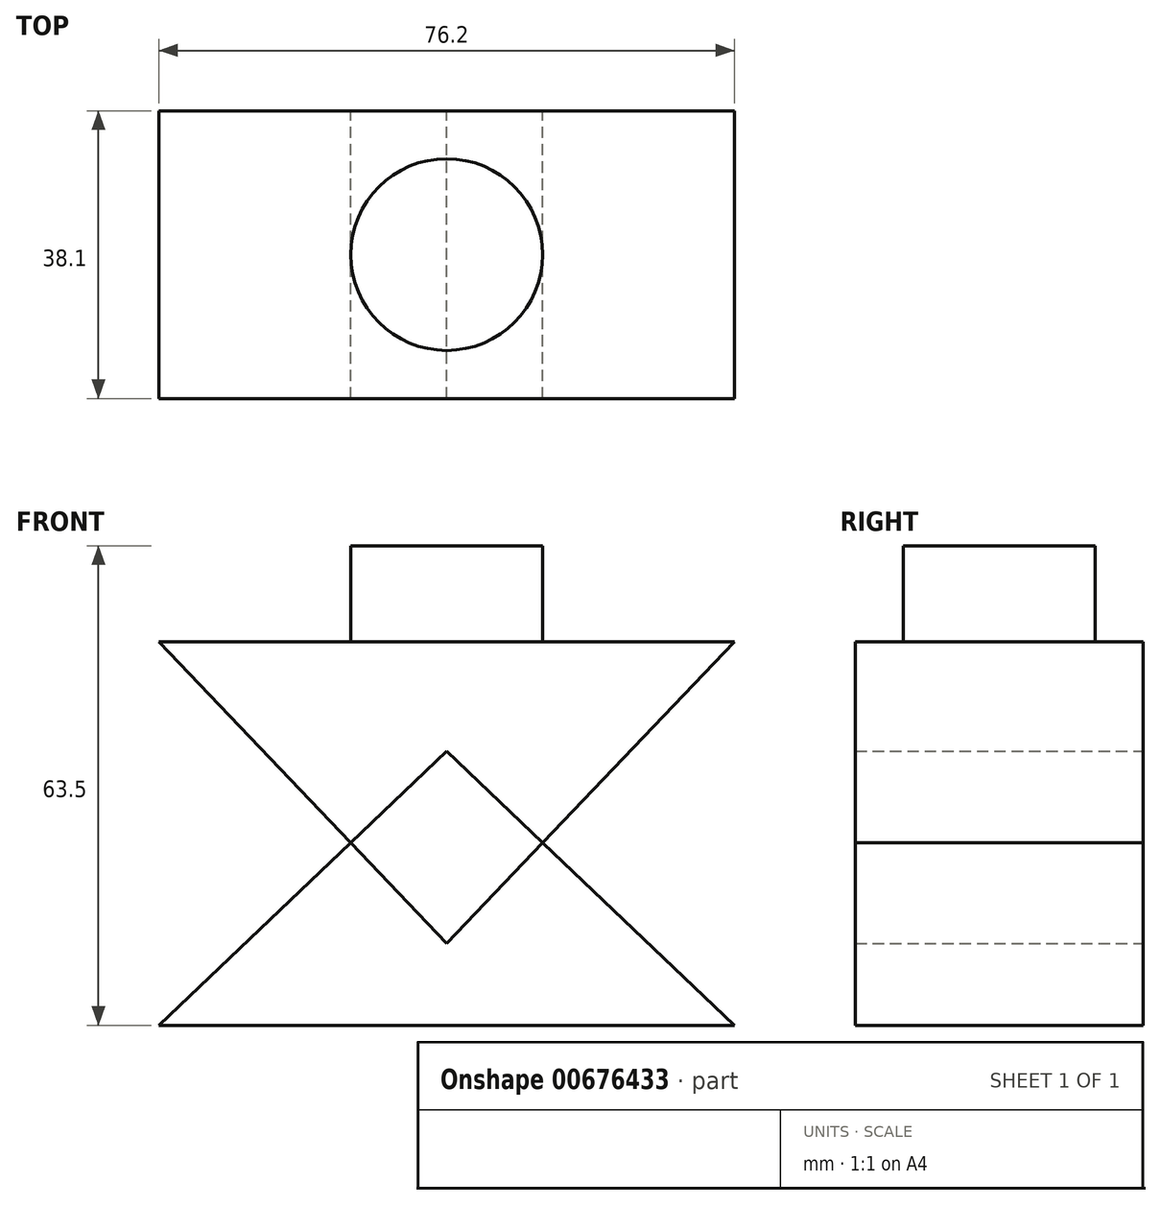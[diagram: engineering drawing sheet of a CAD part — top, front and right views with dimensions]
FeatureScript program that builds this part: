
annotation { "Feature Type Name" : "Feature", "Feature Type Description" : "" }
export const myFeature = defineFeature(function(context is Context, id is Id, definition is map)
    precondition{}
    {
        {
            var Q0;
            Q0=qCreatedBy(makeId("Top.planeOp"),FACE);
            var sketch = newSketch(context, id + "F0", { "sketchPlane" : qUnion([Q0])});
            skCircle(sketch, "E0", {"center": v(0, 0) * mm, "radius": 12.7 * mm});
            skSolve(sketch);
        }
        {
            var Q0;
            Q0 = qSketchRegion(id + "F0", true);
            extrude(context, id + "F1", {"entities" : qUnion([Q0]), "depth" : 12.7 * mm, "offsetDistance" : 25.4 * mm});
        }
        {
            var Q0;
            Q0=makeQuery(id+"F1.opExtrude","SWEPT_BODY",BODY,{"disambiguationData":[OSD([sQuery(id+"F0.wireOp",EDGE,"E0")])]});
            var Q1;
            Q1=makeQuery(id+"F1.opExtrude","SWEPT_FACE",FACE,{"disambiguationData":[OSD([sQuery(id+"F0.wireOp",EDGE,"E0")])]});
            transform(context, id + "F2", {"entities" : qUnion([Q0]), "transformType" : TransformType.TRANSLATION_DISTANCE, "transformDirection" : qUnion([Q1]), "distance" : 50.8 * mm, "oppositeDirection" : true, "makeCopy" : false});
        }
        {
            var Q0;
            Q0=qCreatedBy(makeId("Front.planeOp"),FACE);
            var sketch = newSketch(context, id + "F3", { "sketchPlane" : qUnion([Q0])});
            skLineSegment(sketch, "E1", {"start": v(0, 0) * mm, "end": v(-38.1, 0) * mm});
            skLineSegment(sketch, "E2", {"start": v(0, 0) * mm, "end": v(38.1, 0) * mm});
            skLineSegment(sketch, "E3.MirrorCS", {"start": v(0, 10.82) * mm, "end": v(-38.1, 50.8) * mm});
            skLineSegment(sketch, "E4.MirrorCS", {"start": v(0, 10.82) * mm, "end": v(38.1, 50.8) * mm});
            skLineSegment(sketch, "E5.MirrorCS", {"start": v(0, 50.8) * mm, "end": v(38.1, 50.8) * mm});
            skLineSegment(sketch, "E6.MirrorCS", {"start": v(0, 50.8) * mm, "end": v(-38.1, 50.8) * mm});
            skLineSegment(sketch, "E7", {"start": v(38.1, 0) * mm, "end": v(0, 36.3) * mm});
            skLineSegment(sketch, "E8", {"start": v(0, 36.3) * mm, "end": v(-38.1, 0) * mm});
            skSolve(sketch);
        }
        {
            var Q0;
            {var subQ1=sQuery(id+"F3.wireOp",EDGE,"E5.MirrorCS");Q0=makeQuery(id+"F3.imprint","IMPRINT",FACE,{"disambiguationData":[TD([[makeQuery(id+"F3.imprint","IMPRINT",EDGE,{"derivedFrom":subQ1}),-1.0]])]});}
            var Q1;
            {var subQ8=sQuery(id+"F3.wireOp",EDGE,"E1");Q1=makeQuery(id+"F3.imprint","IMPRINT",FACE,{"disambiguationData":[TD([[makeQuery(id+"F3.imprint","IMPRINT",EDGE,{"derivedFrom":subQ8}),-1.0]])]});}
            extrude(context, id + "F4", {"entities" : qUnion([Q0, Q1]), "operationType" : NewBodyOperationType.ADD, "endBound" : BoundingType.SYMMETRIC, "depth" : 38.1 * mm, "offsetDistance" : 25.4 * mm});
        }
    });
